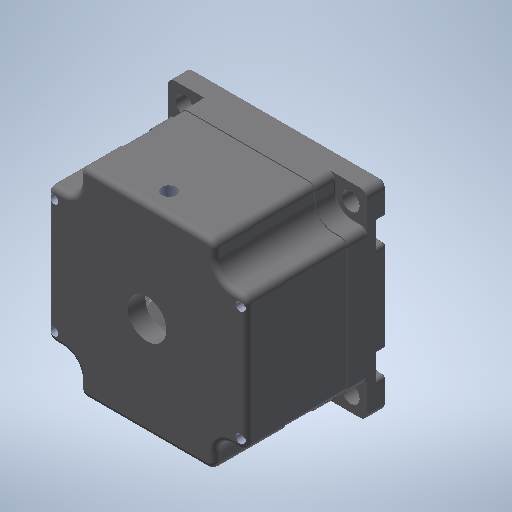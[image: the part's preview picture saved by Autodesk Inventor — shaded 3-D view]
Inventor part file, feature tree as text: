
AUTODESK INVENTOR PART (.ipt)
format: ipt  version: 2025.1 (Build 291241000, 241)  size: 596,480 bytes
history: native  units: mm
features: other x1, imported_body x1, extrude x1, sketch x1
ambient origin geometry x8: Origin, YZ Plane, XZ Plane, XY Plane, X Axis, Y Axis, Z Axis, Center Point
bodies: Body1 (feature_tree)
feature tree (4):
  other  "NEMA 23 - 41mm"
  imported_body  "Base1"
  extrude  "Extrusion1"  Depth=2.0mm
  sketch  "Sketch1"  dims[d3=0.0mm d4=0.0mm d6=2.0mm d7=5.85mm d8=2.0mm]
